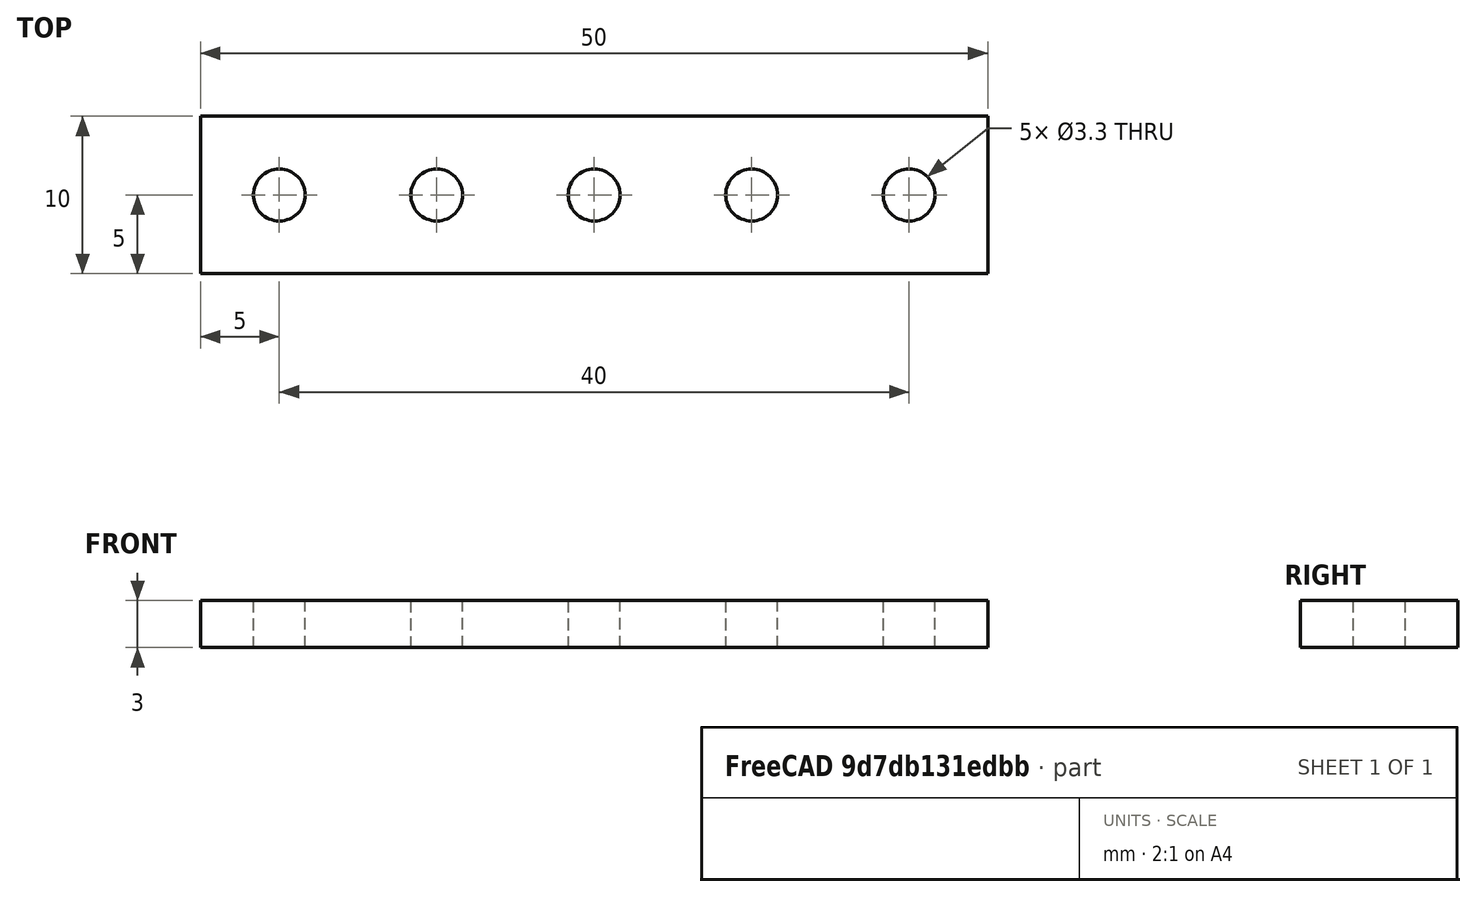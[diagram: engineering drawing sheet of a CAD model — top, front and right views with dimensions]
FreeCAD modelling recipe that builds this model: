
FCSTD DOCUMENT  (FreeCAD 0.20R29177 +233 (Git))
Label: Pieza-de-mecano
License: Creative Commons Attribution-ShareAlike
LicenseURL: http://creativecommons.org/licenses/by-sa/4.0/
objects: Sketcher::SketchObject×1, Part::Extrusion×1
note: 2 computed .brp shape members not serialized (recipe doc carries the construction recipe); baked Part::Feature solids carry a one-line shape summary decoded from their .brp

FEATURE [Sketcher::SketchObject] Sketch
  FullyConstrained = true
  sketch-geometry (9):
    g0: LineSegment StartX=-25 StartY=5 StartZ=0 EndX=25 EndY=5 EndZ=0
    g1: LineSegment StartX=25 StartY=5 StartZ=0 EndX=25 EndY=-5 EndZ=0
    g2: LineSegment StartX=25 StartY=-5 StartZ=0 EndX=-25 EndY=-5 EndZ=0
    g3: LineSegment StartX=-25 StartY=-5 StartZ=0 EndX=-25 EndY=5 EndZ=0
    g4: Circle CenterX=0 CenterY=0 CenterZ=0 NormalX=0 NormalY=0 NormalZ=1 AngleXU=0 Radius=1.65
    g5: Circle CenterX=-10 CenterY=0 CenterZ=0 NormalX=0 NormalY=0 NormalZ=1 AngleXU=0 Radius=1.65
    g6: Circle CenterX=10 CenterY=0 CenterZ=0 NormalX=0 NormalY=0 NormalZ=1 AngleXU=0 Radius=1.65
    g7: Circle CenterX=-20 CenterY=0 CenterZ=0 NormalX=0 NormalY=0 NormalZ=1 AngleXU=0 Radius=1.65
    g8: Circle CenterX=20 CenterY=0 CenterZ=0 NormalX=0 NormalY=0 NormalZ=1 AngleXU=0 Radius=1.65
  constraints (23):
    c: Coincident(g0,g1)
    c: Coincident(g1,g2)
    c: Coincident(g2,g3)
    c: Coincident(g3,g0)
    c: Horizontal(g0)
    c: Horizontal(g2)
    c: Vertical(g1)
    c: Vertical(g3)
    c: Symmetric(g0,g1,g-1)
    c: DistanceY(g1,g1) = 10
    c: DistanceX(g0,g0) = 50
    c: Coincident(g4,g-1)
    c: Diameter(g4) = 3.3
    c: Equal(g5,g4)
    c: Distance(g5,g4) = 10
    c: PointOnObject(g5,g-1)
    c: Equal(g6,g4)
    c: Symmetric(g6,g5,g4)
    c: Equal(g7,g4)
    c: Distance(g7,g5) = 10
    c: PointOnObject(g7,g-1)
    c: Equal(g8,g4)
    c: Symmetric(g8,g7,g4)
FEATURE [Part::Extrusion] Extrude
  Base = -> Sketch
  Dir = (0,0,1)
  DirMode = 2
  FaceMakerClass = Part::FaceMakerBullseye
  LengthFwd = 3
  LengthRev = 0
  Solid = true
  Symmetric = false
